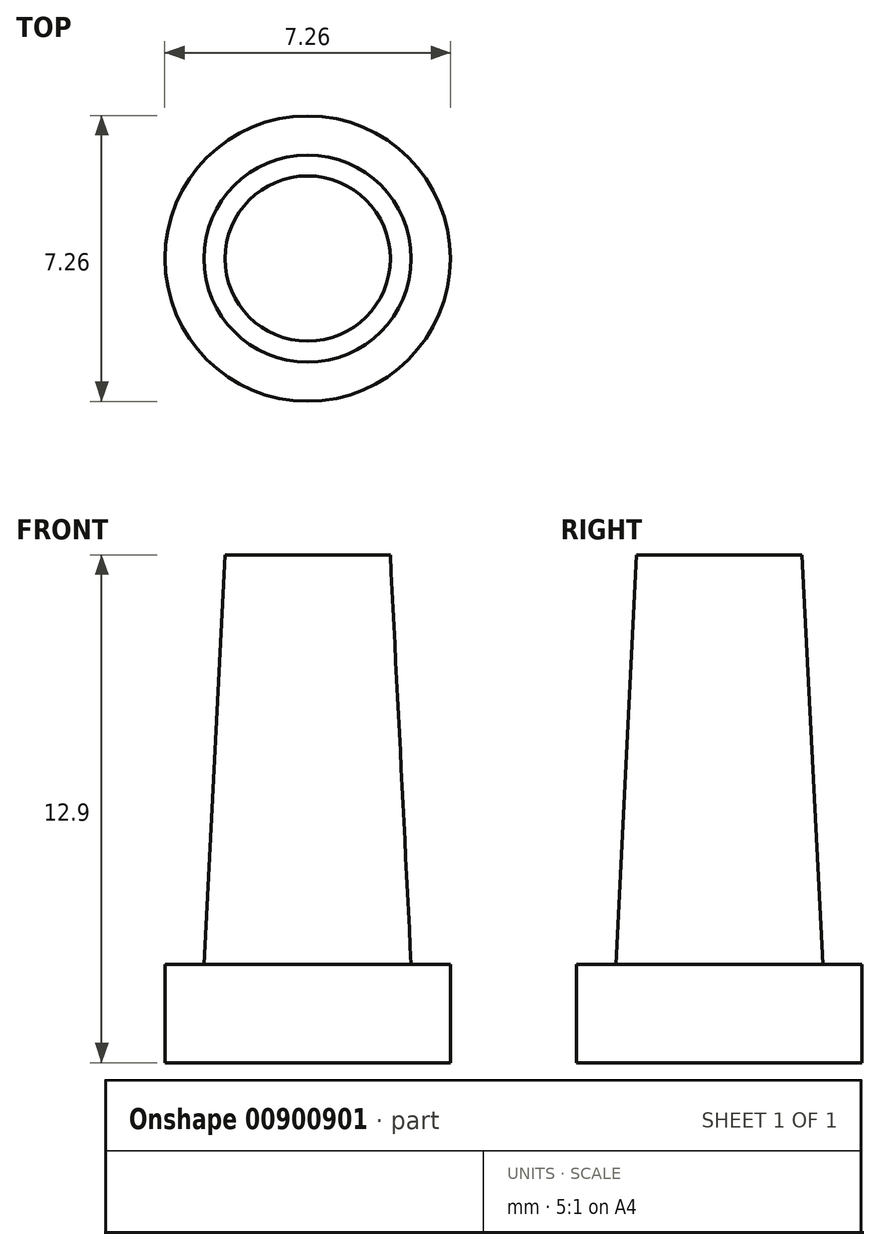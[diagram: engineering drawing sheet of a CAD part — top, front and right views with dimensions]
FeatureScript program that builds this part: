
annotation { "Feature Type Name" : "Feature", "Feature Type Description" : "" }
export const myFeature = defineFeature(function(context is Context, id is Id, definition is map)
    precondition{}
    {
        {
            var Q0;
            Q0=qCreatedBy(makeId("Right.planeOp"),FACE);
            var sketch = newSketch(context, id + "F0", { "sketchPlane" : qUnion([Q0])});
            skLineSegment(sketch, "E0", {"start": v(0, 0) * mm, "end": v(3.62, 0) * mm});
            skLineSegment(sketch, "E1", {"start": v(3.62, 0) * mm, "end": v(3.62, 2.5) * mm});
            skLineSegment(sketch, "E2", {"start": v(3.62, 2.5) * mm, "end": v(2.63, 2.5) * mm});
            skLineSegment(sketch, "E3", {"start": v(2.63, 2.5) * mm, "end": v(2.1, 12.9) * mm});
            skLineSegment(sketch, "E4", {"start": v(2.1, 12.9) * mm, "end": v(0, 12.9) * mm});
            skLineSegment(sketch, "E5", {"start": v(0, 12.9) * mm, "end": v(0, 0) * mm});
            skSolve(sketch);
        }
        {
            var Q0;
            Q0 = qSketchRegion(id + "F0", true);
            var Q1;
            Q1=sQuery(id+"F0.wireOp",EDGE,"E5");
            revolve(context, id + "F1", {"surfaceOperationType" : NewSurfaceOperationType.NEW, "entities" : qUnion([Q0]), "axis" : qUnion([Q1]), "revolveType" : RevolveType.FULL});
        }
    });
